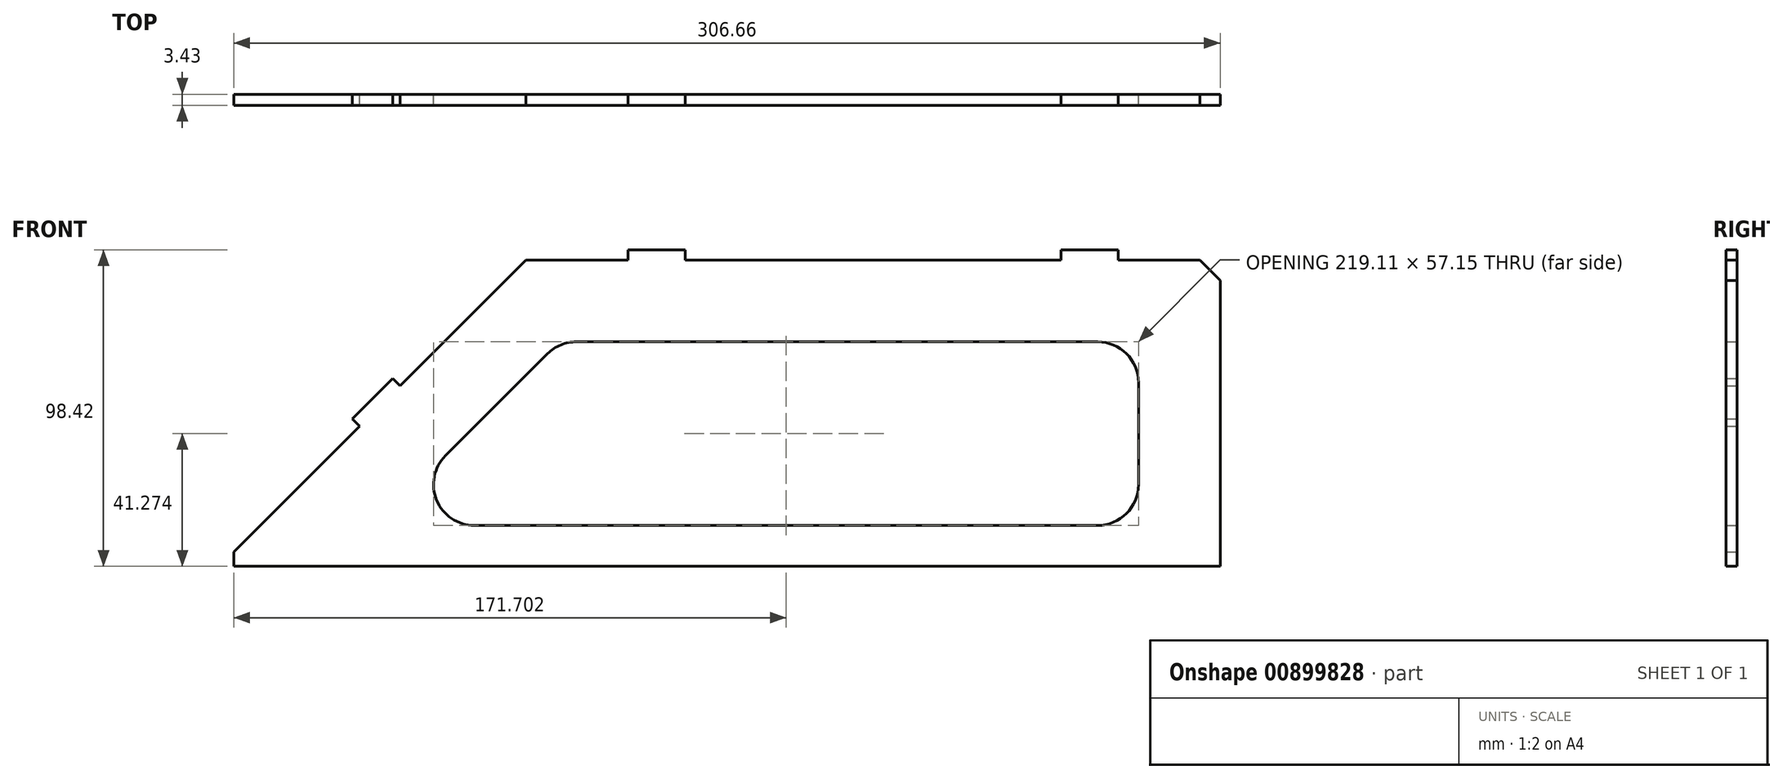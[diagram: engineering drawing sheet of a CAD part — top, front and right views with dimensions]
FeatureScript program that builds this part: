
annotation { "Feature Type Name" : "Feature", "Feature Type Description" : "" }
export const myFeature = defineFeature(function(context is Context, id is Id, definition is map)
    precondition{}
    {
        {
            var Q0;
            Q0=qCreatedBy(makeId("Front.planeOp"),FACE);
            var sketch = newSketch(context, id + "F0", { "sketchPlane" : qUnion([Q0])});
            skArc(sketch, "E0", {"start": v(846.72, -576.75) * mm, "mid": v(855.7, -573.03) * mm, "end": v(859.42, -564.05) * mm});
            skLineSegment(sketch, "E1", {"start": v(859.42, -564.05) * mm, "end": v(859.42, -532.3) * mm});
            skArc(sketch, "E2", {"start": v(859.42, -532.3) * mm, "mid": v(855.7, -523.32) * mm, "end": v(846.72, -519.6) * mm});
            skLineSegment(sketch, "E3", {"start": v(846.72, -519.6) * mm, "end": v(684.7, -519.6) * mm});
            skArc(sketch, "E4", {"start": v(684.7, -519.6) * mm, "mid": v(679.84, -520.57) * mm, "end": v(675.72, -523.32) * mm});
            skLineSegment(sketch, "E5", {"start": v(675.72, -523.32) * mm, "end": v(643.97, -555.07) * mm});
            skArc(sketch, "E6", {"start": v(643.97, -555.07) * mm, "mid": v(641.21, -568.91) * mm, "end": v(652.95, -576.75) * mm});
            skLineSegment(sketch, "E7", {"start": v(652.95, -576.75) * mm, "end": v(846.72, -576.75) * mm});
            skLineSegment(sketch, "E8", {"start": v(700.67, -491.03) * mm, "end": v(700.67, -494.2) * mm});
            skLineSegment(sketch, "E9", {"start": v(718.45, -491.03) * mm, "end": v(700.67, -491.03) * mm});
            skLineSegment(sketch, "E10", {"start": v(718.45, -494.2) * mm, "end": v(718.45, -491.03) * mm});
            skLineSegment(sketch, "E11", {"start": v(835.29, -491.03) * mm, "end": v(835.29, -494.2) * mm});
            skLineSegment(sketch, "E12", {"start": v(853.07, -491.03) * mm, "end": v(835.29, -491.03) * mm});
            skLineSegment(sketch, "E13", {"start": v(853.07, -494.2) * mm, "end": v(853.07, -491.03) * mm});
            skLineSegment(sketch, "E14", {"start": v(884.82, -500.55) * mm, "end": v(878.47, -494.2) * mm});
            skLineSegment(sketch, "E15", {"start": v(578.16, -584.96) * mm, "end": v(578.16, -589.45) * mm});
            skLineSegment(sketch, "E16", {"start": v(615, -543.62) * mm, "end": v(617.25, -545.87) * mm});
            skLineSegment(sketch, "E17", {"start": v(627.58, -531.05) * mm, "end": v(615, -543.62) * mm});
            skLineSegment(sketch, "E18", {"start": v(629.82, -533.3) * mm, "end": v(627.58, -531.05) * mm});
            skLineSegment(sketch, "E19", {"start": v(884.82, -589.45) * mm, "end": v(884.82, -500.55) * mm});
            skLineSegment(sketch, "E20", {"start": v(578.16, -589.45) * mm, "end": v(884.82, -589.45) * mm});
            skLineSegment(sketch, "E21", {"start": v(668.92, -494.2) * mm, "end": v(629.82, -533.3) * mm});
            skLineSegment(sketch, "E22", {"start": v(700.67, -494.2) * mm, "end": v(668.92, -494.2) * mm});
            skLineSegment(sketch, "E23", {"start": v(835.29, -494.2) * mm, "end": v(718.45, -494.2) * mm});
            skLineSegment(sketch, "E24", {"start": v(878.47, -494.2) * mm, "end": v(853.07, -494.2) * mm});
            skLineSegment(sketch, "E25", {"start": v(617.25, -545.87) * mm, "end": v(578.16, -584.96) * mm});
            skSolve(sketch);
        }
        {
            var Q0;
            Q0 = qSketchRegion(id + "F0", true);
            extrude(context, id + "F1", {"entities" : qUnion([Q0]), "depth" : 3.43 * mm, "offsetDistance" : 25.4 * mm});
        }
    });
